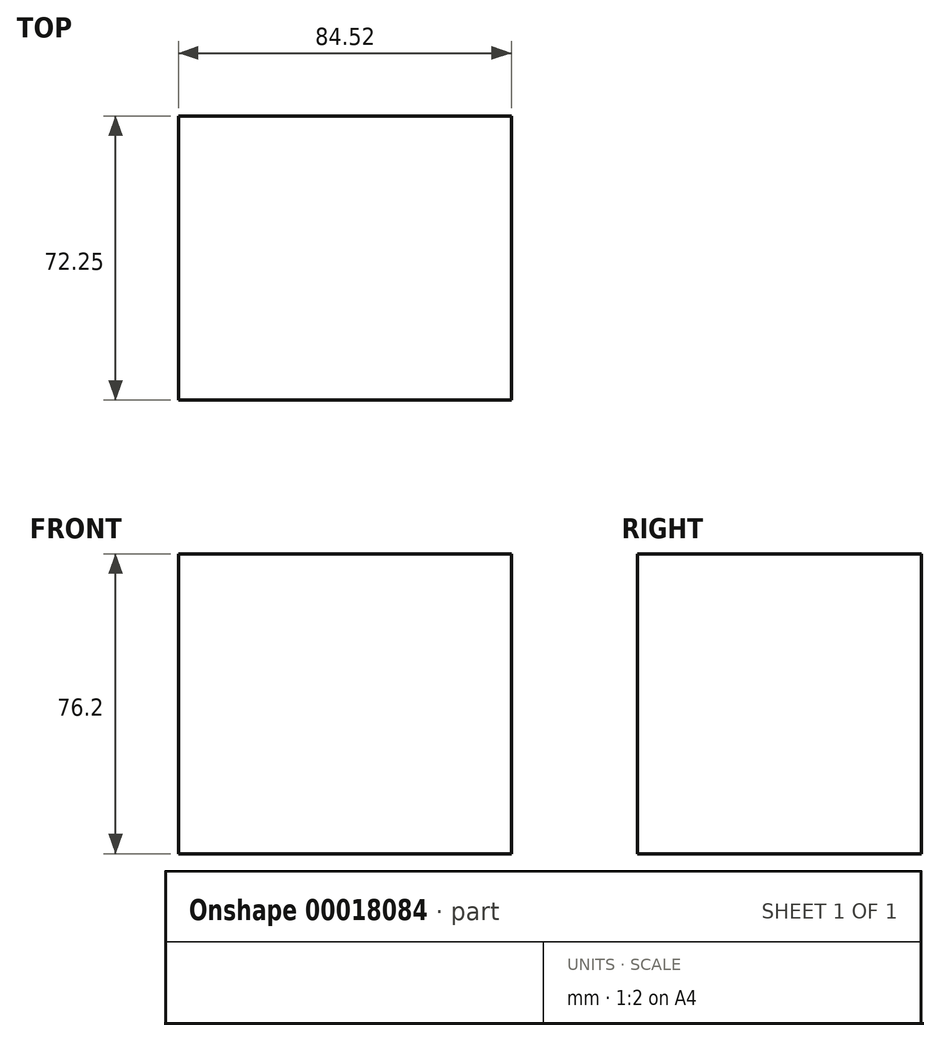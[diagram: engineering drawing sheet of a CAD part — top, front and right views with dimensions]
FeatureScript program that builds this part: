
annotation { "Feature Type Name" : "Feature", "Feature Type Description" : "" }
export const myFeature = defineFeature(function(context is Context, id is Id, definition is map)
    precondition{}
    {
        {
            var Q0;
            Q0=qCreatedBy(makeId("Front.planeOp"),FACE);
            var sketch = newSketch(context, id + "F0", { "sketchPlane" : qUnion([Q0])});
            skLineSegment(sketch, "E0.bottom", {"start": v(49.81, 55.38) * mm, "end": v(-34.71, 55.38) * mm});
            skLineSegment(sketch, "E0.top", {"start": v(49.81, -20.82) * mm, "end": v(-34.71, -20.82) * mm});
            skLineSegment(sketch, "E0.left", {"start": v(49.81, 55.38) * mm, "end": v(49.81, -20.82) * mm});
            skLineSegment(sketch, "E0.right", {"start": v(-34.71, 55.38) * mm, "end": v(-34.71, -20.82) * mm});
            skSolve(sketch);
        }
        {
            var Q0;
            Q0=makeQuery(id+"F0.imprint","IMPRINT",FACE,{"disambiguationData":[TD([[makeQuery(id+"F0.imprint","IMPRINT",EDGE,{"derivedFrom":sQuery(id+"F0.wireOp",EDGE,"E0.bottom")}),1.0]])]});
            extrude(context, id + "F1", {"entities" : qUnion([Q0]), "depth" : 72.25 * mm});
        }
    });
